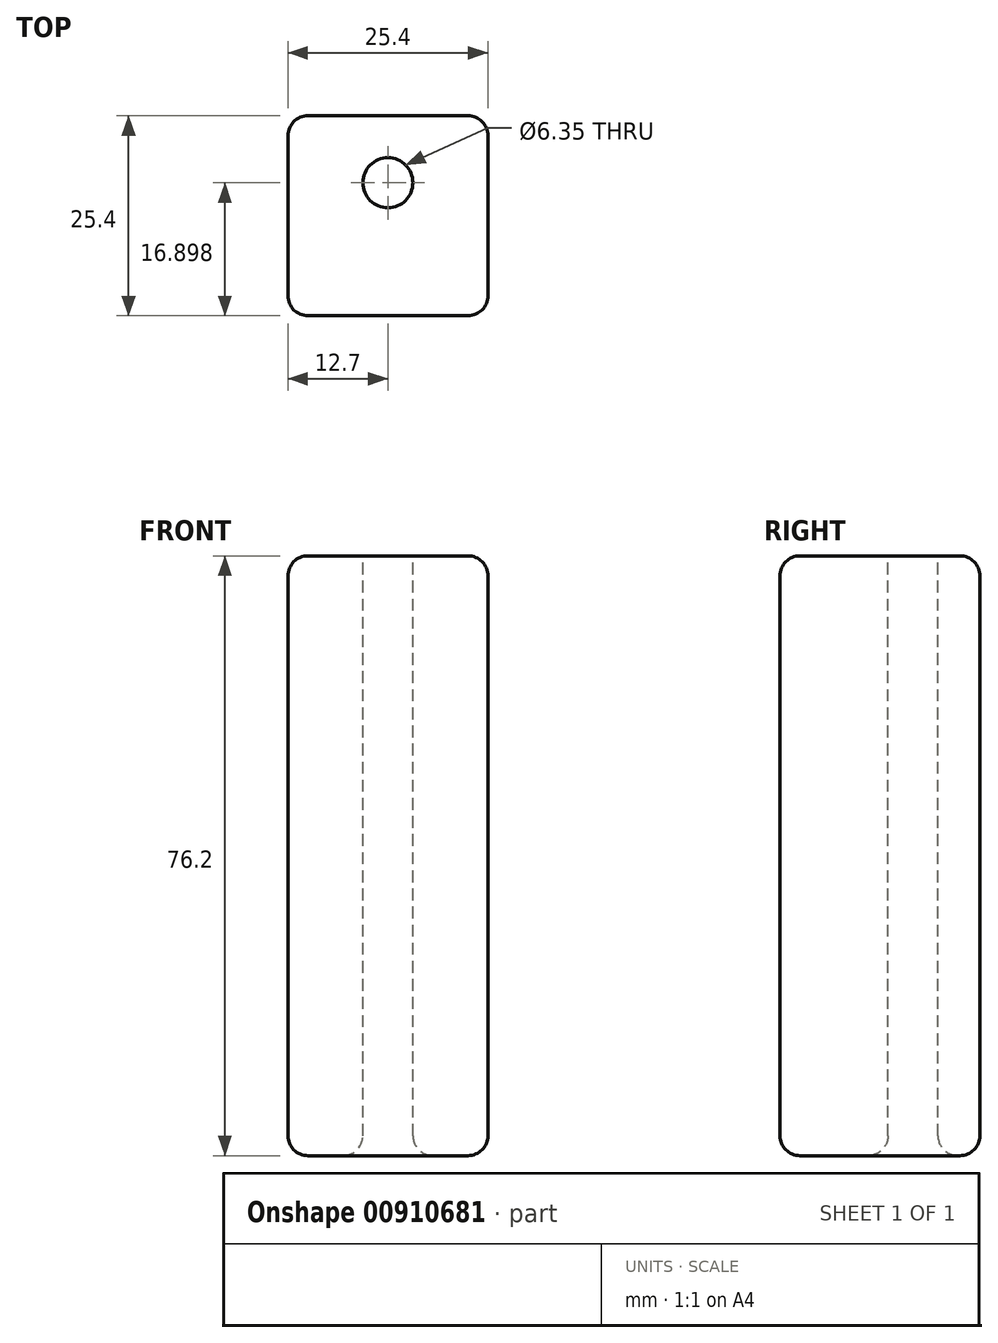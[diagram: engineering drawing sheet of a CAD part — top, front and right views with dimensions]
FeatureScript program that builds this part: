
annotation { "Feature Type Name" : "Feature", "Feature Type Description" : "" }
export const myFeature = defineFeature(function(context is Context, id is Id, definition is map)
    precondition{}
    {
        {
            var Q0;
            Q0=qCreatedBy(makeId("Front.planeOp"),FACE);
            var sketch = newSketch(context, id + "F0", { "sketchPlane" : qUnion([Q0])});
            skLineSegment(sketch, "E0.bottom", {"start": v(12.7, 38.1) * mm, "end": v(-12.7, 38.1) * mm});
            skLineSegment(sketch, "E0.top", {"start": v(12.7, -38.1) * mm, "end": v(-12.7, -38.1) * mm});
            skLineSegment(sketch, "E0.left", {"start": v(12.7, 38.1) * mm, "end": v(12.7, -38.1) * mm});
            skLineSegment(sketch, "E0.right", {"start": v(-12.7, 38.1) * mm, "end": v(-12.7, -38.1) * mm});
            skPoint(sketch, "E0.middle", {"position": v(0, 0) * mm});
            skSolve(sketch);
        }
        {
            var Q0;
            Q0=makeQuery(id+"F0.imprint","IMPRINT",FACE,{"disambiguationData":[TD([[makeQuery(id+"F0.imprint","IMPRINT",EDGE,{"derivedFrom":sQuery(id+"F0.wireOp",EDGE,"E0.bottom")}),1.0]])]});
            extrude(context, id + "F1", {"entities" : qUnion([Q0]), "depth" : 25.4 * mm, "offsetDistance" : 25.4 * mm});
        }
        {
            var Q0;
            Q0=makeQuery(id+"F1.opExtrude","SWEPT_FACE",FACE,{"disambiguationData":[OSD([sQuery(id+"F0.wireOp",EDGE,"E0.bottom")])]});
            var sketch = newSketch(context, id + "F2", { "sketchPlane" : qUnion([Q0])});
            skCircle(sketch, "E1", {"center": v(0, -8.5) * mm, "radius": 3.18 * mm});
            skSolve(sketch);
        }
        {
            var Q0;
            Q0=qSketchRegion(id+"F2",true);
            var sketch = newSketch(context, id + "F3", { "sketchPlane" : qUnion([Q0])});
            skSolve(sketch);
        }
        {
            var Q0;
            Q0=makeQuery(id+"F3.imprint","IMPRINT",FACE,{"disambiguationData":[TD([[makeQuery(id+"F3.imprint","IMPRINT",EDGE,{"derivedFrom":makeQuery(id+"F2.imprint","IMPRINT",EDGE,{"derivedFrom":sQuery(id+"F2.wireOp",EDGE,"E1")})}),1.0]])]});
            extrude(context, id + "F4", {"entities" : qUnion([Q0]), "operationType" : NewBodyOperationType.REMOVE, "endBound" : BoundingType.THROUGH_ALL, "oppositeDirection" : true, "depth" : 25.4 * mm, "offsetDistance" : 25.4 * mm});
        }
        {
            var Q0;
            Q0=makeQuery(id+"F1.opExtrude","SWEPT_EDGE",EDGE,{"disambiguationData":[OSD([sQuery(id+"F0.wireOp",EDGE,"E0.bottom"),sQuery(id+"F0.wireOp",EDGE,"E0.left")])]});
            var Q1;
            Q1=makeQuery(id+"F1.opExtrude","CAP_EDGE",EDGE,{"disambiguationData":[OSD([sQuery(id+"F0.wireOp",EDGE,"E0.bottom")])],"isStart":false});
            var Q2;
            Q2=makeQuery(id+"F1.opExtrude","SWEPT_EDGE",EDGE,{"disambiguationData":[OSD([sQuery(id+"F0.wireOp",EDGE,"E0.bottom"),sQuery(id+"F0.wireOp",EDGE,"E0.right")])]});
            var Q3;
            Q3=makeQuery(id+"F1.opExtrude","CAP_EDGE",EDGE,{"disambiguationData":[OSD([sQuery(id+"F0.wireOp",EDGE,"E0.left")])],"isStart":false});
            var Q4;
            Q4=makeQuery(id+"F1.opExtrude","CAP_EDGE",EDGE,{"disambiguationData":[OSD([sQuery(id+"F0.wireOp",EDGE,"E0.right")])],"isStart":false});
            var Q5;
            Q5=makeQuery(id+"F1.opExtrude","CAP_EDGE",EDGE,{"disambiguationData":[OSD([sQuery(id+"F0.wireOp",EDGE,"E0.right")])],"isStart":true});
            var Q6;
            Q6=makeQuery(id+"F4.boolean.opBoolean","INTERSECT",EDGE,{"derivedFrom":[makeQuery(id+"F1.opExtrude","SWEPT_FACE",FACE,{"disambiguationData":[OSD([sQuery(id+"F0.wireOp",EDGE,"E0.top")])]}),makeQuery(id+"F4.opExtrude","SWEPT_FACE",FACE,{"disambiguationData":[OSD([sQuery(id+"F2.wireOp",EDGE,"E1")])]})]});
            var Q7;
            Q7=makeQuery(id+"F4.boolean.opBoolean","COPY",EDGE,{"derivedFrom":makeQuery(id+"F4.opExtrude","CAP_EDGE",EDGE,{"disambiguationData":[OSD([sQuery(id+"F2.wireOp",EDGE,"E1")])],"isStart":true})});
            var Q8;
            Q8=makeQuery(id+"F1.opExtrude","CAP_EDGE",EDGE,{"disambiguationData":[OSD([sQuery(id+"F0.wireOp",EDGE,"E0.bottom")])],"isStart":true});
            var Q9;
            Q9=makeQuery(id+"F1.opExtrude","CAP_EDGE",EDGE,{"disambiguationData":[OSD([sQuery(id+"F0.wireOp",EDGE,"E0.left")])],"isStart":true});
            var Q10;
            Q10=makeQuery(id+"F1.opExtrude","CAP_EDGE",EDGE,{"disambiguationData":[OSD([sQuery(id+"F0.wireOp",EDGE,"E0.top")])],"isStart":true});
            var Q11;
            Q11=makeQuery(id+"F1.opExtrude","SWEPT_EDGE",EDGE,{"disambiguationData":[OSD([sQuery(id+"F0.wireOp",EDGE,"E0.top"),sQuery(id+"F0.wireOp",EDGE,"E0.left")])]});
            var Q12;
            Q12=makeQuery(id+"F1.opExtrude","CAP_EDGE",EDGE,{"disambiguationData":[OSD([sQuery(id+"F0.wireOp",EDGE,"E0.top")])],"isStart":false});
            var Q13;
            Q13=makeQuery(id+"F1.opExtrude","SWEPT_EDGE",EDGE,{"disambiguationData":[OSD([sQuery(id+"F0.wireOp",EDGE,"E0.top"),sQuery(id+"F0.wireOp",EDGE,"E0.right")])]});
            fillet(context, id + "F5", {"entities" : qUnion([Q0, Q1, Q2, Q3, Q4, Q5, Q6, Q7, Q8, Q9, Q10, Q11, Q12, Q13]), "radius" : 2.54 * mm, "tangentPropagation" : true, "allowEdgeOverflow" : false});
        }
    });
